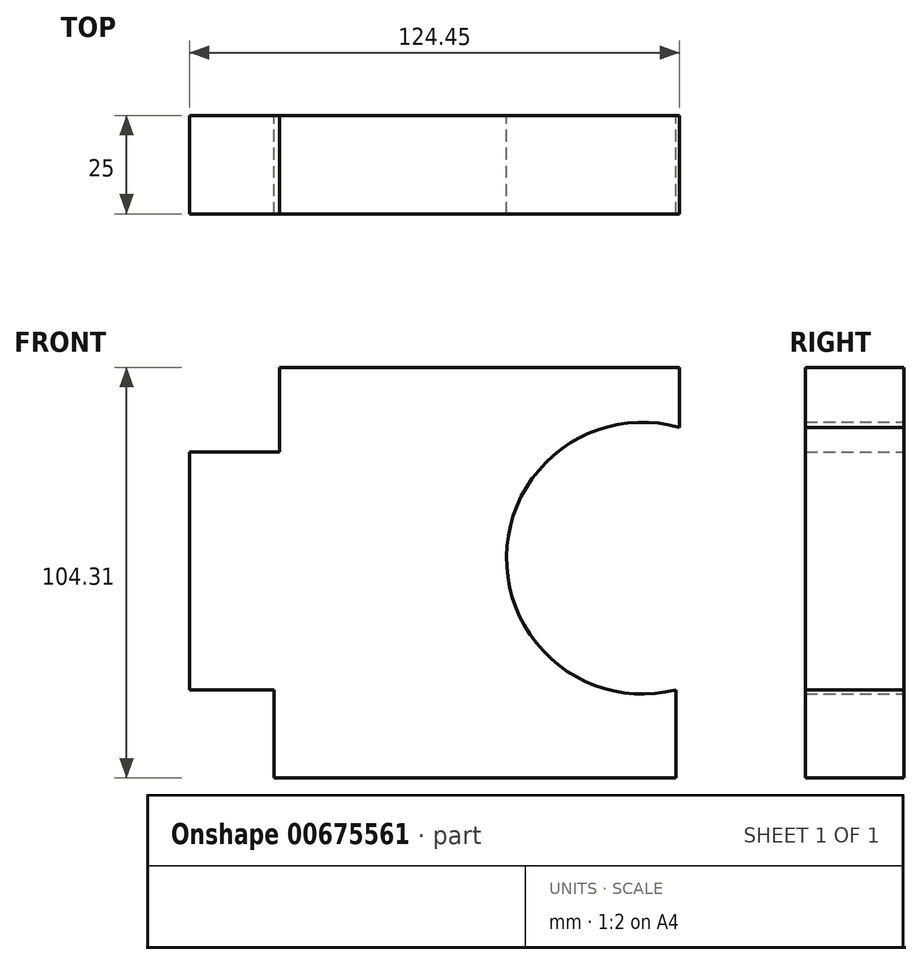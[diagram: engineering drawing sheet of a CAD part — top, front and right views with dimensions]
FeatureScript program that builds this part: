
annotation { "Feature Type Name" : "Feature", "Feature Type Description" : "" }
export const myFeature = defineFeature(function(context is Context, id is Id, definition is map)
    precondition{}
    {
        {
            var Q0;
            Q0=qCreatedBy(makeId("Front.planeOp"),FACE);
            var sketch = newSketch(context, id + "F0", { "sketchPlane" : qUnion([Q0])});
            skLineSegment(sketch, "E0", {"start": v(-56.63, 51.93) * mm, "end": v(44.99, 51.93) * mm});
            skLineSegment(sketch, "E1", {"start": v(44.99, 51.93) * mm, "end": v(44.99, 36.7) * mm});
            skLineSegment(sketch, "E2", {"start": v(-56.63, 51.93) * mm, "end": v(-56.63, 30.44) * mm});
            skLineSegment(sketch, "E3", {"start": v(-56.63, 30.44) * mm, "end": v(-79.46, 30.44) * mm});
            skLineSegment(sketch, "E4", {"start": v(-79.46, 30.44) * mm, "end": v(-79.46, -30) * mm});
            skLineSegment(sketch, "E5", {"start": v(-79.46, -30) * mm, "end": v(-57.97, -30) * mm});
            skLineSegment(sketch, "E6", {"start": v(-57.97, -30) * mm, "end": v(-57.97, -52.38) * mm});
            skLineSegment(sketch, "E7", {"start": v(-57.97, -52.38) * mm, "end": v(44.1, -52.38) * mm});
            skLineSegment(sketch, "E8", {"start": v(44.1, -52.38) * mm, "end": v(44.1, -30) * mm});
            skArc(sketch, "E9", {"start": v(44.99, 36.7) * mm, "mid": v(1.06, 3.94) * mm, "end": v(44.1, -30) * mm});
            skSolve(sketch);
        }
        {
            var Q0;
            Q0 = qSketchRegion(id + "F0", true);
            extrude(context, id + "F1", {"entities" : qUnion([Q0]), "depth" : 25 * mm, "offsetDistance" : 25 * mm});
        }
    });
